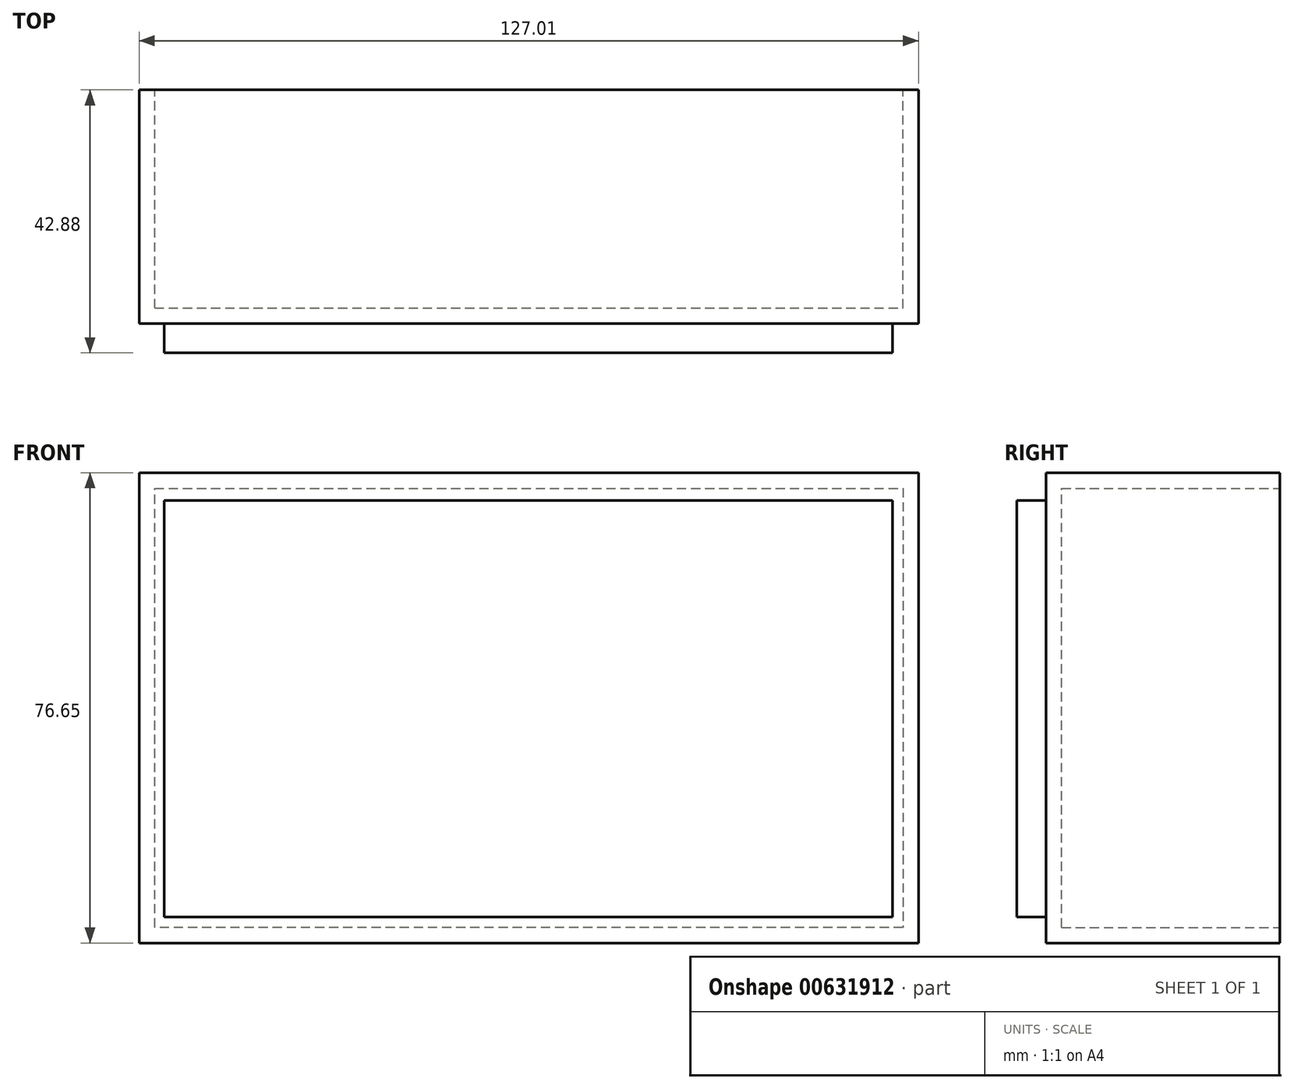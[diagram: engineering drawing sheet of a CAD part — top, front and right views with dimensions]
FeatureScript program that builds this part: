
annotation { "Feature Type Name" : "Feature", "Feature Type Description" : "" }
export const myFeature = defineFeature(function(context is Context, id is Id, definition is map)
    precondition{}
    {
        {
            var Q0;
            Q0=qCreatedBy(makeId("Front.planeOp"),FACE);
            var sketch = newSketch(context, id + "F0", { "sketchPlane" : qUnion([Q0])});
            skLineSegment(sketch, "E0", {"start": v(-60.29, 44.62) * mm, "end": v(66.72, 44.62) * mm});
            skLineSegment(sketch, "E1", {"start": v(66.72, 44.62) * mm, "end": v(66.72, -32.03) * mm});
            skLineSegment(sketch, "E2", {"start": v(66.72, -32.03) * mm, "end": v(-60.29, -32.03) * mm});
            skLineSegment(sketch, "E3", {"start": v(-60.29, -32.03) * mm, "end": v(-60.29, 44.62) * mm});
            skSolve(sketch);
        }
        {
            var Q0;
            Q0=makeQuery(id+"F0.imprint","IMPRINT",FACE,{"disambiguationData":[TD([[makeQuery(id+"F0.imprint","IMPRINT",EDGE,{"derivedFrom":sQuery(id+"F0.wireOp",EDGE,"E0")}),-1.0]])]});
            extrude(context, id + "F1", {"entities" : qUnion([Q0]), "depth" : 38.1 * mm, "offsetDistance" : 25.4 * mm});
        }
        {
            var Q0;
            Q0=makeQuery(id+"F1.opExtrude","CAP_FACE",FACE,{"disambiguationData":[OSD([sQuery(id+"F0.wireOp",EDGE,"E0"),sQuery(id+"F0.wireOp",EDGE,"E1"),sQuery(id+"F0.wireOp",EDGE,"E2"),sQuery(id+"F0.wireOp",EDGE,"E3")])],"isStart":true});
            shell(context, id + "F2", {"entities" : qUnion([Q0]), "thickness" : 2.54 * mm});
        }
        {
            var Q0;
            Q0=makeQuery(id+"F1.opExtrude","CAP_FACE",FACE,{"disambiguationData":[OSD([sQuery(id+"F0.wireOp",EDGE,"E0"),sQuery(id+"F0.wireOp",EDGE,"E1"),sQuery(id+"F0.wireOp",EDGE,"E2"),sQuery(id+"F0.wireOp",EDGE,"E3")])],"isStart":false});
            var sketch = newSketch(context, id + "F3", { "sketchPlane" : qUnion([Q0])});
            skLineSegment(sketch, "E4.bottom", {"start": v(-56.21, 40.1) * mm, "end": v(62.47, 40.1) * mm});
            skLineSegment(sketch, "E4.top", {"start": v(-56.21, -27.83) * mm, "end": v(62.47, -27.83) * mm});
            skLineSegment(sketch, "E4.left", {"start": v(-56.21, 40.1) * mm, "end": v(-56.21, -27.83) * mm});
            skLineSegment(sketch, "E4.right", {"start": v(62.47, 40.1) * mm, "end": v(62.47, -27.83) * mm});
            skSolve(sketch);
        }
        {
            var Q0;
            Q0=makeQuery(id+"F3.imprint","IMPRINT",FACE,{"disambiguationData":[TD([[makeQuery(id+"F3.imprint","IMPRINT",EDGE,{"derivedFrom":sQuery(id+"F3.wireOp",EDGE,"E4.bottom")}),-1.0]])]});
            extrude(context, id + "F4", {"entities" : qUnion([Q0]), "operationType" : NewBodyOperationType.ADD, "depth" : 4.78 * mm, "offsetDistance" : 25.4 * mm});
        }
    });
